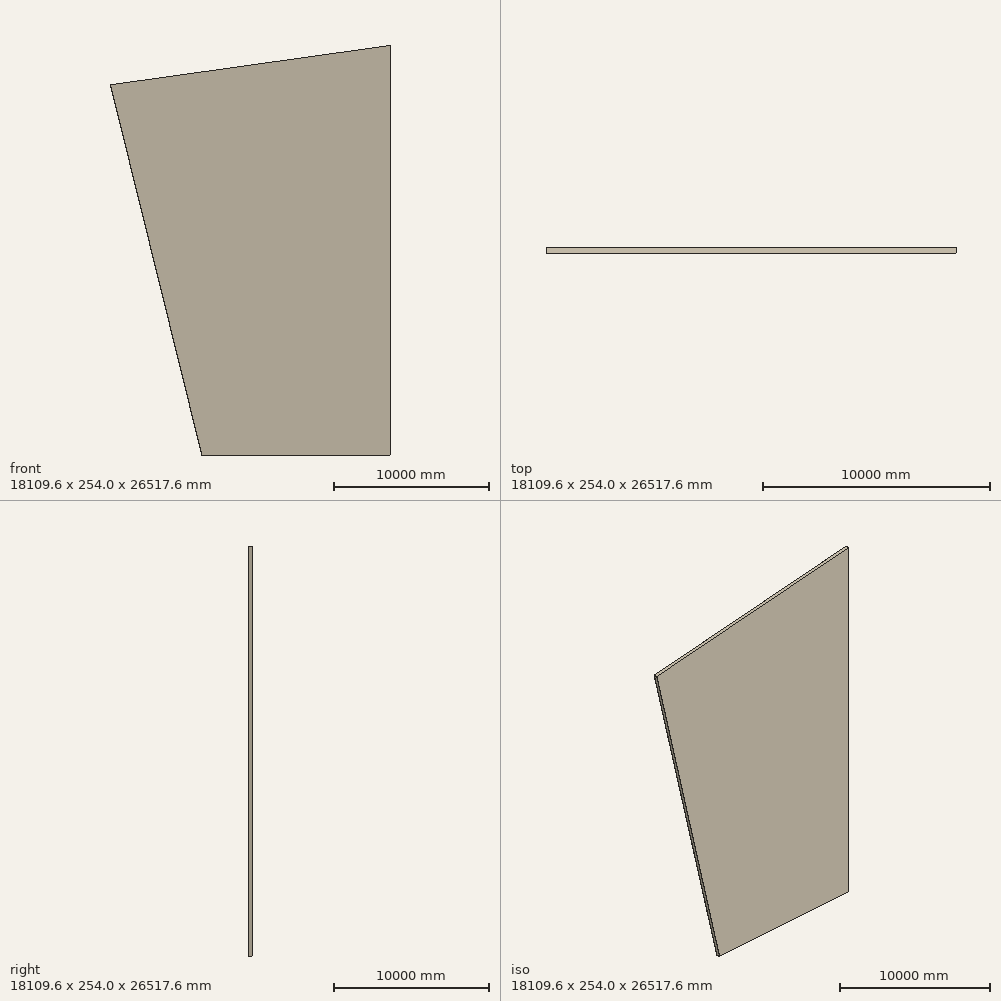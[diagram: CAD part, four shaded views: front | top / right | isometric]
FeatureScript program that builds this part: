
annotation { "Feature Type Name" : "Feature", "Feature Type Description" : "" }
export const myFeature = defineFeature(function(context is Context, id is Id, definition is map)
    precondition{}
    {
        {
            var Q0;
            Q0=qCreatedBy(makeId("Front.planeOp"),FACE);
            var sketch = newSketch(context, id + "F0", { "sketchPlane" : qUnion([Q0])});
            skLineSegment(sketch, "E0", {"start": v(11470.52, -1143.04) * mm, "end": v(-721.48, -1143.04) * mm});
            skLineSegment(sketch, "E1", {"start": v(-721.48, -1143.04) * mm, "end": v(-6639.04, 22826.09) * mm});
            skLineSegment(sketch, "E2", {"start": v(-6639.04, 22826.09) * mm, "end": v(11470.52, 25374.56) * mm});
            skLineSegment(sketch, "E3", {"start": v(11470.52, 25374.56) * mm, "end": v(11470.52, -1143.04) * mm});
            skSolve(sketch);
        }
        {
            var Q0;
            Q0 = qSketchRegion(id + "F0", true);
            extrude(context, id + "F1", {"entities" : qUnion([Q0]), "depth" : 254 * mm, "offsetDistance" : 25.4 * mm});
        }
    });
